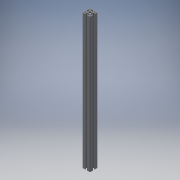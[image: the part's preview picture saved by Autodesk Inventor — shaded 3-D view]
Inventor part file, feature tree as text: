
AUTODESK INVENTOR PART (.ipt)
format: ipt  version: 2018 (Build 220112000, 112)  size: 232,448 bytes
history: native  units: mm
features: other x42, sketch x5, hole x4, extrude x1
ambient origin geometry x8: Origin, YZ Plane, XZ Plane, XY Plane, X Axis, Y Axis, Z Axis, Center Point
bodies: Solid1 (feature_tree)
feature tree (52):
  extrude  "Extrusion1"  [1 undecoded]
  hole  "Drilling 1"  [1 undecoded]
  hole  "Drilling 2"  [1 undecoded]
  hole  "Drilling 3"  [1 undecoded]
  hole  "Drilling 4"  [1 undecoded]
  other  "side_4d_XY"
  other  "side_4d_YZ"
  other  "side_4d_ZX"
  other  "side_4d_X"
  other  "side_4d_Y"
  other  "side_4d_Z"
  other  "side_4d_Center"
  other  "side_1a_XY"
  other  "side_1a_YZ"
  other  "side_1a_ZX"
  other  "side_1a_X"
  other  "side_1a_Y"
  other  "side_1a_Z"
  other  "side_1a_Center"
  other  "side_2b_XY"
  other  "side_2b_YZ"
  other  "side_2b_ZX"
  other  "side_2b_X"
  other  "side_2b_Y"
  other  "side_2b_Z"
  other  "side_2b_Center"
  other  "side_3c_XY"
  other  "side_3c_YZ"
  other  "side_3c_ZX"
  other  "side_3c_X"
  other  "side_3c_Y"
  other  "side_3c_Z"
  other  "side_3c_Center"
  other  "end_XY"
  other  "end_YZ"
  other  "end_ZX"
  other  "end_X"
  other  "end_Y"
  other  "end_Z"
  other  "end_Center"
  other  "start_XY"
  other  "start_YZ"
  other  "start_ZX"
  other  "start_X"
  other  "start_Y"
  other  "start_Z"
  other  "start_Center"
  sketch  "Skizze_1"  dims[d0=700.0mm d1=0.0mm]
  sketch  "Sketch2"  dims[d2=5.0mm d3=6.0mm d4=4.0mm d5=2.0mm d6=90.0deg d7=6000.0mm d8=0.0mm]
  sketch  "Sketch3"  dims[d9=5.0mm d10=6.0mm d11=4.0mm d12=2.0mm d13=90.0deg d14=6000.0mm d15=0.0mm]
  sketch  "Sketch4"  dims[d16=5.0mm d17=6.0mm d18=4.0mm d19=2.0mm d20=90.0deg d21=6000.0mm d22=0.0mm]
  sketch  "Sketch5"  dims[d23=5.0mm d24=6.0mm d25=4.0mm d26=2.0mm d27=90.0deg d28=6000.0mm d29=0.0mm]
note: 5 required parameter values undecoded (feature->parameter linkage not recoverable at this tier; creation-order binding heuristic only, values carry confidence <= 0.55)
